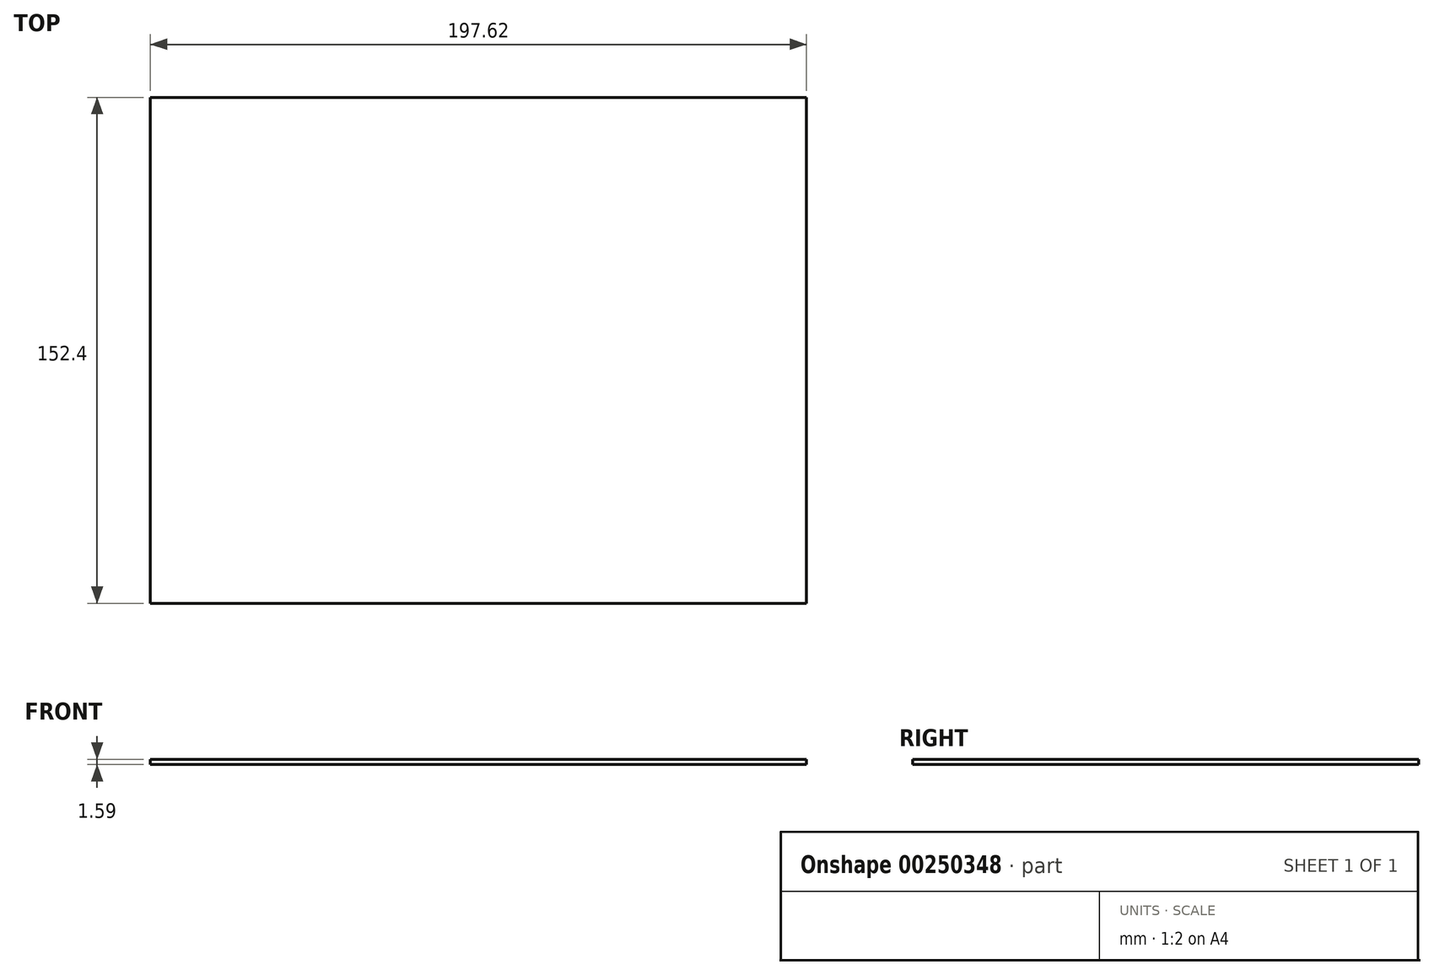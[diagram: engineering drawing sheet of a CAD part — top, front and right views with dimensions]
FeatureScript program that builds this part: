
annotation { "Feature Type Name" : "Feature", "Feature Type Description" : "" }
export const myFeature = defineFeature(function(context is Context, id is Id, definition is map)
    precondition{}
    {
        {
            var Q0;
            Q0=qCreatedBy(makeId("Top.planeOp"),FACE);
            var sketch = newSketch(context, id + "F0", { "sketchPlane" : qUnion([Q0])});
            skLineSegment(sketch, "E0.bottom", {"start": v(98.8, 76.2) * mm, "end": v(-98.8, 76.2) * mm});
            skLineSegment(sketch, "E0.top", {"start": v(98.8, -76.2) * mm, "end": v(-98.8, -76.2) * mm});
            skLineSegment(sketch, "E0.left", {"start": v(98.8, 76.2) * mm, "end": v(98.8, -76.2) * mm});
            skLineSegment(sketch, "E0.right", {"start": v(-98.8, 76.2) * mm, "end": v(-98.8, -76.2) * mm});
            skPoint(sketch, "E0.middle", {"position": v(0, 0) * mm});
            skSolve(sketch);
        }
        {
            var Q0;
            Q0 = qSketchRegion(id + "F0", true);
            extrude(context, id + "F1", {"entities" : qUnion([Q0]), "depth" : 1.59 * mm});
        }
    });
